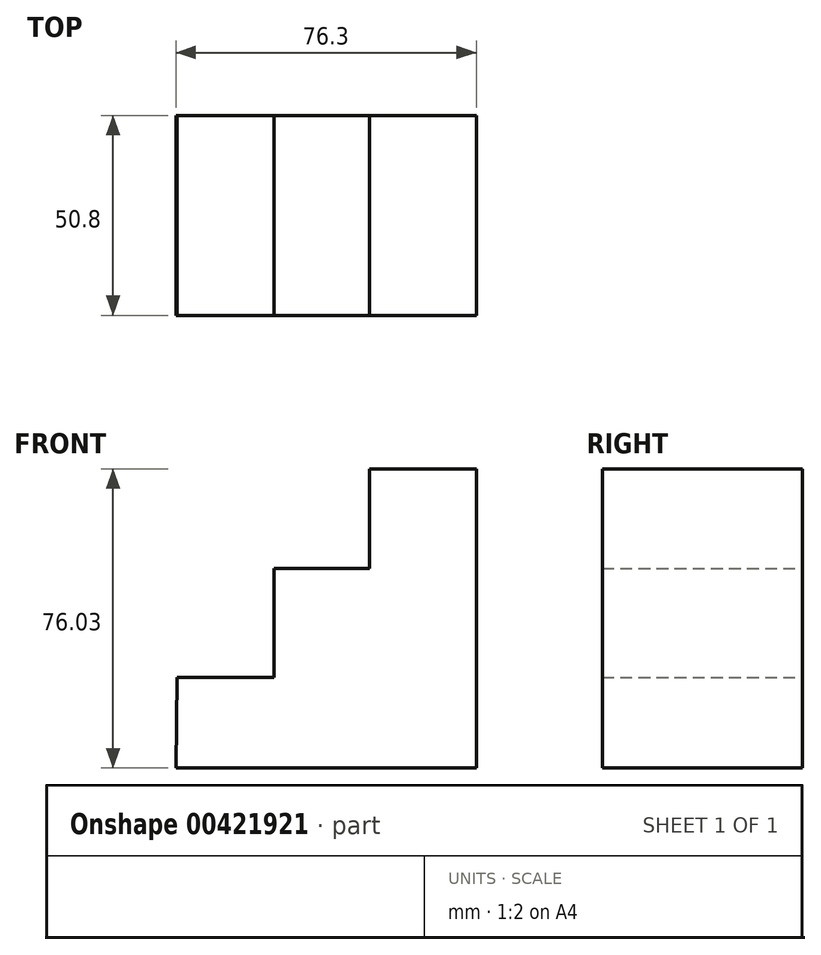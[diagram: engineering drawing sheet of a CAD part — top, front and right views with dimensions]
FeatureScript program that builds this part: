
annotation { "Feature Type Name" : "Feature", "Feature Type Description" : "" }
export const myFeature = defineFeature(function(context is Context, id is Id, definition is map)
    precondition{}
    {
        {
            var Q0;
            Q0=qCreatedBy(makeId("Front.planeOp"),FACE);
            var sketch = newSketch(context, id + "F0", { "sketchPlane" : qUnion([Q0])});
            skLineSegment(sketch, "E0", {"start": v(-42, -27.58) * mm, "end": v(34.3, -27.58) * mm});
            skLineSegment(sketch, "E1", {"start": v(34.3, -27.58) * mm, "end": v(34.3, 48.45) * mm});
            skLineSegment(sketch, "E2", {"start": v(34.3, 48.45) * mm, "end": v(7.14, 48.45) * mm});
            skLineSegment(sketch, "E3", {"start": v(7.14, 48.45) * mm, "end": v(7.14, 23.2) * mm});
            skLineSegment(sketch, "E4", {"start": v(7.14, 23.2) * mm, "end": v(-17.05, 23.2) * mm});
            skLineSegment(sketch, "E5", {"start": v(-17.05, 23.2) * mm, "end": v(-17.05, -4.53) * mm});
            skLineSegment(sketch, "E6", {"start": v(-17.05, -4.53) * mm, "end": v(-41.72, -4.53) * mm});
            skLineSegment(sketch, "E7", {"start": v(-41.72, -4.53) * mm, "end": v(-42, -27.58) * mm});
            skSolve(sketch);
        }
        {
            var Q0;
            Q0 = qSketchRegion(id + "F0", true);
            extrude(context, id + "F1", {"entities" : qUnion([Q0]), "depth" : 50.8 * mm});
        }
    });
